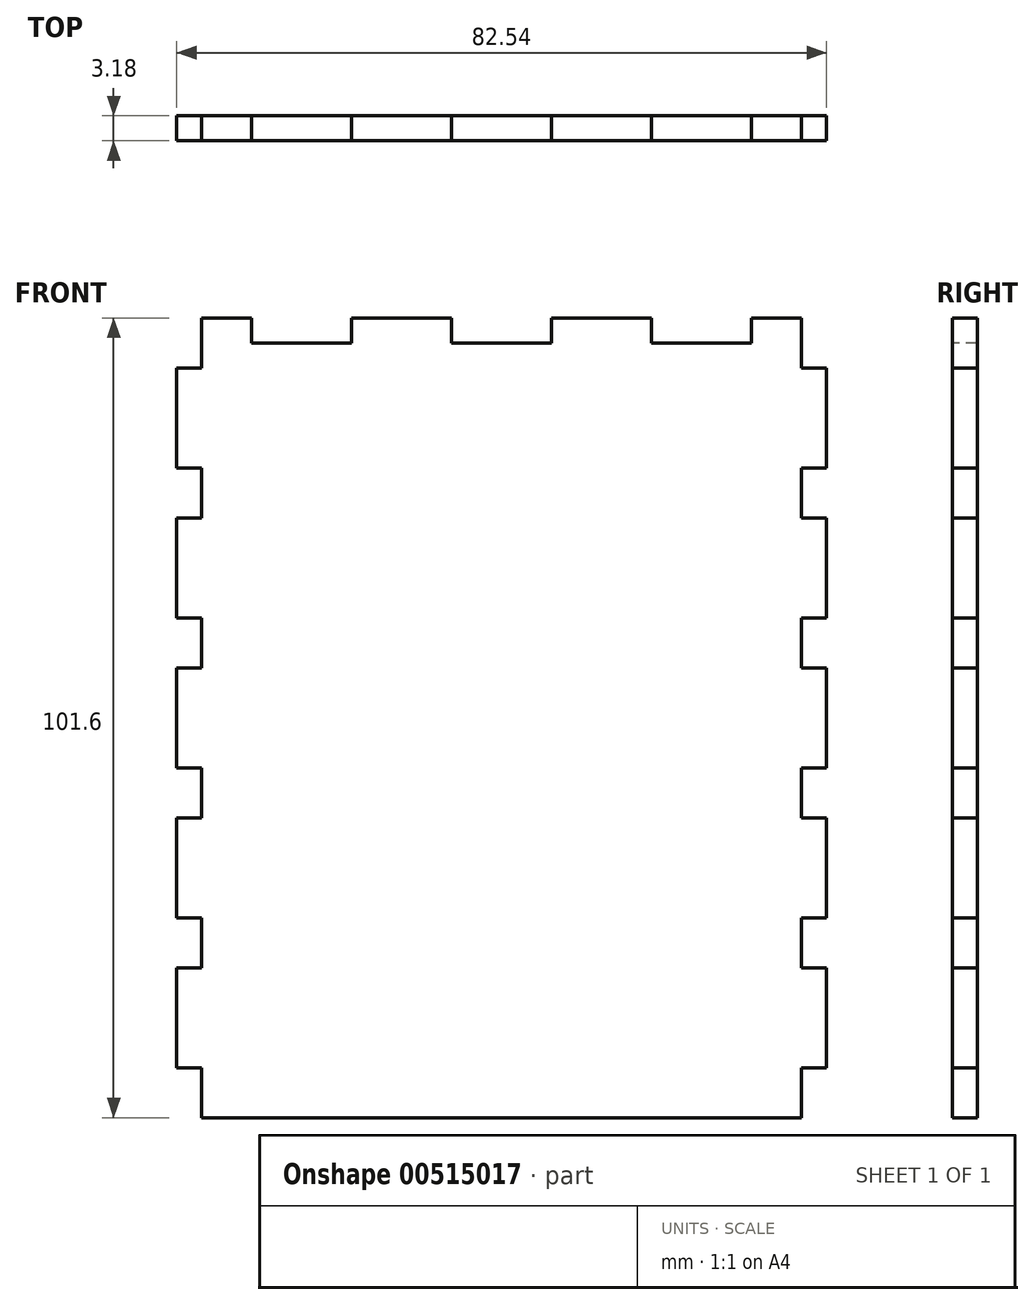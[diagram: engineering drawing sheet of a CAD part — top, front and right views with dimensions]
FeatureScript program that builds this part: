
annotation { "Feature Type Name" : "Feature", "Feature Type Description" : "" }
export const myFeature = defineFeature(function(context is Context, id is Id, definition is map)
    precondition{}
    {
        {
            var Q0;
            Q0=qCreatedBy(makeId("Front.planeOp"),FACE);
            var sketch = newSketch(context, id + "F0", { "sketchPlane" : qUnion([Q0])});
            skLineSegment(sketch, "E0.bottom", {"start": v(-41.28, 50.8) * mm, "end": v(41.27, 50.8) * mm});
            skLineSegment(sketch, "E0.top", {"start": v(-41.27, -50.8) * mm, "end": v(41.28, -50.8) * mm});
            skLineSegment(sketch, "E0.left", {"start": v(-41.28, 50.8) * mm, "end": v(-41.27, -50.8) * mm});
            skLineSegment(sketch, "E0.right", {"start": v(41.27, 50.8) * mm, "end": v(41.28, -50.8) * mm});
            skSolve(sketch);
        }
        {
            var Q0;
            Q0=makeQuery(id+"F0.imprint","IMPRINT",FACE,{"disambiguationData":[TD([[makeQuery(id+"F0.imprint","IMPRINT",EDGE,{"derivedFrom":sQuery(id+"F0.wireOp",EDGE,"E0.bottom")}),-1.0]])]});
            extrude(context, id + "F1", {"entities" : qUnion([Q0]), "depth" : 3.17 * mm, "offsetDistance" : 25.4 * mm});
        }
        {
            var Q0;
            Q0=makeQuery(id+"F1.opExtrude","CAP_FACE",FACE,{"disambiguationData":[OSD([sQuery(id+"F0.wireOp",EDGE,"E0.bottom"),sQuery(id+"F0.wireOp",EDGE,"E0.top"),sQuery(id+"F0.wireOp",EDGE,"E0.left"),sQuery(id+"F0.wireOp",EDGE,"E0.right")])],"isStart":false});
            var sketch = newSketch(context, id + "F2", { "sketchPlane" : qUnion([Q0])});
            skLineSegment(sketch, "E1.bottom", {"start": v(-41.27, -50.8) * mm, "end": v(-38.1, -50.8) * mm});
            skLineSegment(sketch, "E1.top", {"start": v(-41.28, -44.45) * mm, "end": v(-38.1, -44.45) * mm});
            skLineSegment(sketch, "E1.left", {"start": v(-41.27, -50.8) * mm, "end": v(-41.27, -44.45) * mm});
            skLineSegment(sketch, "E1.right", {"start": v(-38.1, -50.8) * mm, "end": v(-38.1, -44.45) * mm});
            skLineSegment(sketch, "E2.0.1.0", {"start": v(-41.28, -25.4) * mm, "end": v(-38.1, -25.4) * mm});
            skLineSegment(sketch, "E2.0.1.1", {"start": v(-41.27, -31.75) * mm, "end": v(-38.1, -31.75) * mm});
            skLineSegment(sketch, "E2.0.1.2", {"start": v(-41.27, -31.75) * mm, "end": v(-41.27, -25.4) * mm});
            skLineSegment(sketch, "E2.0.1.3", {"start": v(-38.1, -31.75) * mm, "end": v(-38.1, -25.4) * mm});
            skLineSegment(sketch, "E2.0.2.0", {"start": v(-41.28, -6.35) * mm, "end": v(-38.1, -6.35) * mm});
            skLineSegment(sketch, "E2.0.2.1", {"start": v(-41.27, -12.7) * mm, "end": v(-38.1, -12.7) * mm});
            skLineSegment(sketch, "E2.0.2.2", {"start": v(-41.27, -12.7) * mm, "end": v(-41.27, -6.35) * mm});
            skLineSegment(sketch, "E2.0.2.3", {"start": v(-38.1, -12.7) * mm, "end": v(-38.1, -6.35) * mm});
            skLineSegment(sketch, "E2.0.3.0", {"start": v(-41.28, 12.7) * mm, "end": v(-38.1, 12.7) * mm});
            skLineSegment(sketch, "E2.0.3.1", {"start": v(-41.27, 6.35) * mm, "end": v(-38.1, 6.35) * mm});
            skLineSegment(sketch, "E2.0.3.2", {"start": v(-41.27, 6.35) * mm, "end": v(-41.27, 12.7) * mm});
            skLineSegment(sketch, "E2.0.3.3", {"start": v(-38.1, 6.35) * mm, "end": v(-38.1, 12.7) * mm});
            skLineSegment(sketch, "E2.0.4.0", {"start": v(-41.28, 31.75) * mm, "end": v(-38.1, 31.75) * mm});
            skLineSegment(sketch, "E2.0.4.1", {"start": v(-41.27, 25.4) * mm, "end": v(-38.1, 25.4) * mm});
            skLineSegment(sketch, "E2.0.4.2", {"start": v(-41.27, 25.4) * mm, "end": v(-41.27, 31.75) * mm});
            skLineSegment(sketch, "E2.0.4.3", {"start": v(-38.1, 25.4) * mm, "end": v(-38.1, 31.75) * mm});
            skLineSegment(sketch, "E2.0.5.0", {"start": v(-41.28, 50.8) * mm, "end": v(-38.1, 50.8) * mm});
            skLineSegment(sketch, "E2.0.5.1", {"start": v(-41.27, 44.45) * mm, "end": v(-38.1, 44.45) * mm});
            skLineSegment(sketch, "E2.0.5.2", {"start": v(-41.27, 44.45) * mm, "end": v(-41.27, 50.8) * mm});
            skLineSegment(sketch, "E2.0.5.3", {"start": v(-38.1, 44.45) * mm, "end": v(-38.1, 50.8) * mm});
            skLineSegment(sketch, "E2.direction1", {"start": v(-41.27, -50.8) * mm, "end": v(-15.88, -50.8) * mm, "construction": true});
            skLineSegment(sketch, "E2.direction2", {"start": v(-41.27, -50.8) * mm, "end": v(-41.27, -31.75) * mm, "construction": true});
            skLineSegment(sketch, "E3", {"start": v(0, 50.8) * mm, "end": v(0, -50.8) * mm, "construction": true});
            skLineSegment(sketch, "E4.MirrorCS", {"start": v(41.28, -50.8) * mm, "end": v(38.1, -50.8) * mm});
            skLineSegment(sketch, "E5.MirrorCS", {"start": v(41.27, -12.7) * mm, "end": v(38.1, -12.7) * mm});
            skLineSegment(sketch, "E6.MirrorCS", {"start": v(41.28, -44.45) * mm, "end": v(38.1, -44.45) * mm});
            skLineSegment(sketch, "E7.MirrorCS", {"start": v(41.27, -12.7) * mm, "end": v(41.27, -6.35) * mm});
            skLineSegment(sketch, "E8.MirrorCS", {"start": v(41.28, 12.7) * mm, "end": v(38.1, 12.7) * mm});
            skLineSegment(sketch, "E9.MirrorCS", {"start": v(41.28, -25.4) * mm, "end": v(38.1, -25.4) * mm});
            skLineSegment(sketch, "E10.MirrorCS", {"start": v(41.27, 25.4) * mm, "end": v(38.1, 25.4) * mm});
            skLineSegment(sketch, "E11.MirrorCS", {"start": v(41.28, -50.8) * mm, "end": v(41.28, -44.45) * mm});
            skLineSegment(sketch, "E12.MirrorCS", {"start": v(41.27, -31.75) * mm, "end": v(41.27, -25.4) * mm});
            skLineSegment(sketch, "E13.MirrorCS", {"start": v(41.27, 44.45) * mm, "end": v(38.1, 44.45) * mm});
            skLineSegment(sketch, "E14.MirrorCS", {"start": v(38.1, 44.45) * mm, "end": v(38.1, 50.8) * mm});
            skLineSegment(sketch, "E15.MirrorCS", {"start": v(41.27, 6.35) * mm, "end": v(38.1, 6.35) * mm});
            skLineSegment(sketch, "E16.MirrorCS", {"start": v(41.28, -6.35) * mm, "end": v(38.1, -6.35) * mm});
            skLineSegment(sketch, "E17.MirrorCS", {"start": v(38.1, 6.35) * mm, "end": v(38.1, 12.7) * mm});
            skLineSegment(sketch, "E18.MirrorCS", {"start": v(41.27, 6.35) * mm, "end": v(41.27, 12.7) * mm});
            skLineSegment(sketch, "E19.MirrorCS", {"start": v(41.28, -31.75) * mm, "end": v(38.1, -31.75) * mm});
            skLineSegment(sketch, "E20.MirrorCS", {"start": v(41.27, 44.45) * mm, "end": v(41.27, 50.8) * mm});
            skLineSegment(sketch, "E21.MirrorCS", {"start": v(41.28, 50.8) * mm, "end": v(38.1, 50.8) * mm});
            skLineSegment(sketch, "E22.MirrorCS", {"start": v(41.28, 31.75) * mm, "end": v(38.1, 31.75) * mm});
            skLineSegment(sketch, "E23.MirrorCS", {"start": v(38.1, -12.7) * mm, "end": v(38.1, -6.35) * mm});
            skLineSegment(sketch, "E24.MirrorCS", {"start": v(38.1, -31.75) * mm, "end": v(38.1, -25.4) * mm});
            skLineSegment(sketch, "E25.MirrorCS", {"start": v(38.1, -50.8) * mm, "end": v(38.1, -44.45) * mm});
            skLineSegment(sketch, "E26.MirrorCS", {"start": v(41.27, 25.4) * mm, "end": v(41.27, 31.75) * mm});
            skLineSegment(sketch, "E27.MirrorCS", {"start": v(38.1, 25.4) * mm, "end": v(38.1, 31.75) * mm});
            skLineSegment(sketch, "E28.MirrorCS", {"start": v(41.28, -50.8) * mm, "end": v(15.88, -50.8) * mm, "construction": true});
            skLineSegment(sketch, "E29.MirrorCS", {"start": v(41.28, -50.8) * mm, "end": v(41.28, -31.75) * mm, "construction": true});
            skSolve(sketch);
        }
        {
            var Q0;
            Q0=qSketchRegion(id+"F2",true);
            extrude(context, id + "F3", {"entities" : qUnion([Q0]), "operationType" : NewBodyOperationType.REMOVE, "endBound" : BoundingType.THROUGH_ALL, "oppositeDirection" : true, "depth" : 25.4 * mm, "offsetDistance" : 25.4 * mm});
        }
        {
            var Q0;
            Q0=makeQuery(id+"F1.opExtrude","CAP_FACE",FACE,{"disambiguationData":[OSD([sQuery(id+"F0.wireOp",EDGE,"E0.bottom"),sQuery(id+"F0.wireOp",EDGE,"E0.top"),sQuery(id+"F0.wireOp",EDGE,"E0.left"),sQuery(id+"F0.wireOp",EDGE,"E0.right")])],"isStart":false});
            var sketch = newSketch(context, id + "F4", { "sketchPlane" : qUnion([Q0])});
            skLineSegment(sketch, "E30.bottom", {"start": v(-31.75, 50.8) * mm, "end": v(-19.05, 50.8) * mm});
            skLineSegment(sketch, "E30.top", {"start": v(-31.75, 47.62) * mm, "end": v(-19.05, 47.62) * mm});
            skLineSegment(sketch, "E30.left", {"start": v(-31.75, 50.8) * mm, "end": v(-31.75, 47.62) * mm});
            skLineSegment(sketch, "E30.right", {"start": v(-19.05, 50.8) * mm, "end": v(-19.05, 47.62) * mm});
            skLineSegment(sketch, "E31.1.0.0", {"start": v(-6.35, 50.8) * mm, "end": v(-6.35, 47.62) * mm});
            skLineSegment(sketch, "E31.1.0.1", {"start": v(-6.35, 47.62) * mm, "end": v(6.35, 47.62) * mm});
            skLineSegment(sketch, "E31.1.0.2", {"start": v(6.35, 50.8) * mm, "end": v(6.35, 47.62) * mm});
            skLineSegment(sketch, "E31.1.0.3", {"start": v(-6.35, 50.8) * mm, "end": v(6.35, 50.8) * mm});
            skLineSegment(sketch, "E31.2.0.0", {"start": v(19.05, 50.8) * mm, "end": v(19.05, 47.62) * mm});
            skLineSegment(sketch, "E31.2.0.1", {"start": v(19.05, 47.62) * mm, "end": v(31.75, 47.62) * mm});
            skLineSegment(sketch, "E31.2.0.2", {"start": v(31.75, 50.8) * mm, "end": v(31.75, 47.62) * mm});
            skLineSegment(sketch, "E31.2.0.3", {"start": v(19.05, 50.8) * mm, "end": v(31.75, 50.8) * mm});
            skLineSegment(sketch, "E31.direction1", {"start": v(-31.75, 47.62) * mm, "end": v(-6.35, 47.62) * mm, "construction": true});
            skSolve(sketch);
        }
        {
            var Q0;
            Q0=qSketchRegion(id+"F4",true);
            extrude(context, id + "F5", {"entities" : qUnion([Q0]), "operationType" : NewBodyOperationType.REMOVE, "endBound" : BoundingType.THROUGH_ALL, "oppositeDirection" : true, "depth" : 25.4 * mm, "offsetDistance" : 25.4 * mm});
        }
    });
